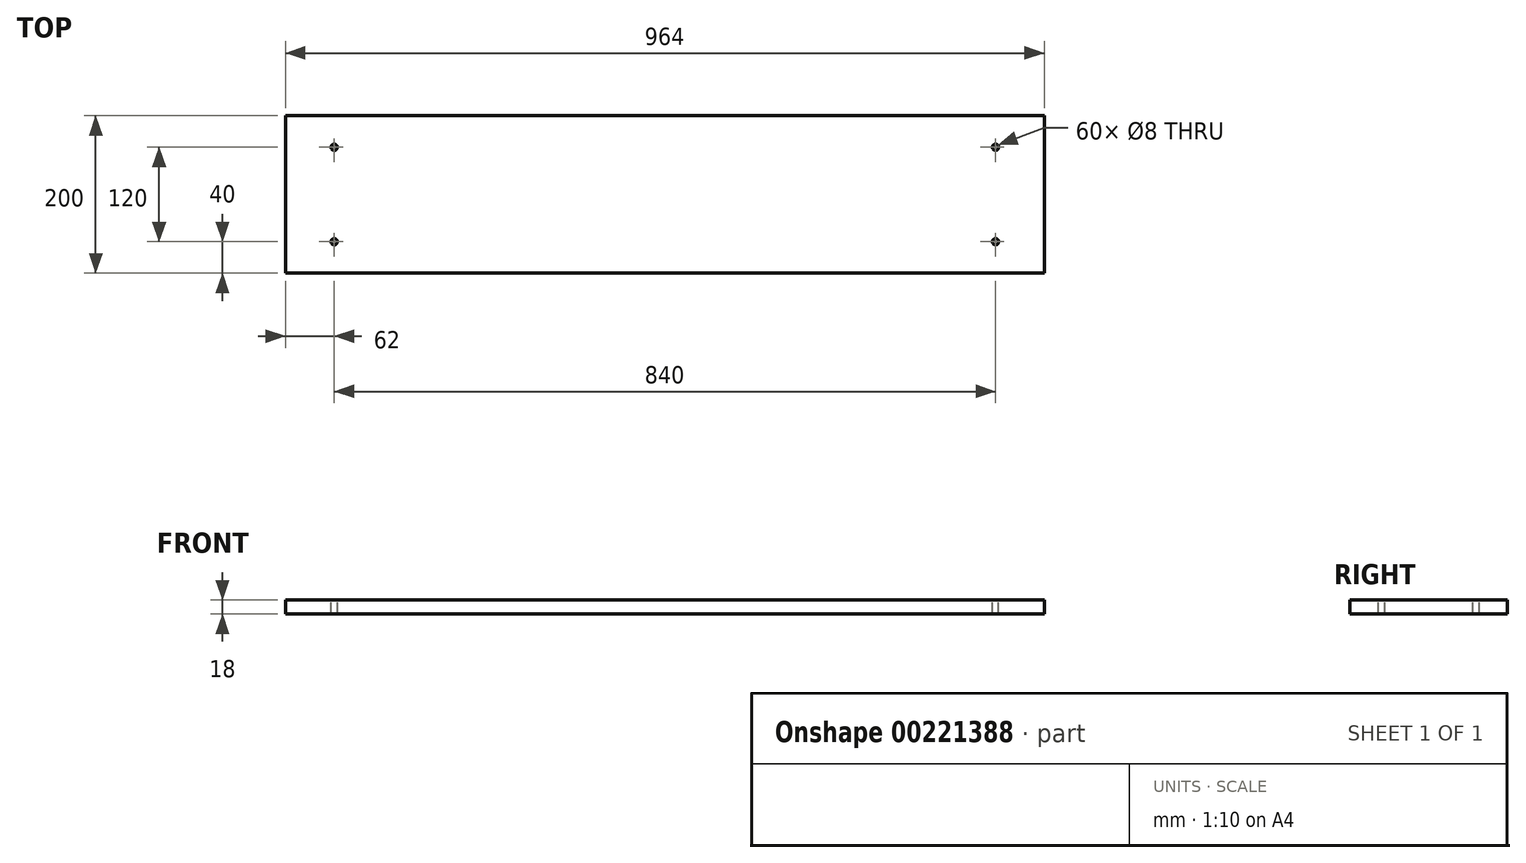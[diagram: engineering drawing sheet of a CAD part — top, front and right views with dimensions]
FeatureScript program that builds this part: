
annotation { "Feature Type Name" : "Feature", "Feature Type Description" : "" }
export const myFeature = defineFeature(function(context is Context, id is Id, definition is map)
    precondition{}
    {
        {
            var Q0;
            Q0=qCreatedBy(makeId("Top.planeOp"),FACE);
            var sketch = newSketch(context, id + "F0", { "sketchPlane" : qUnion([Q0])});
            skLineSegment(sketch, "E0.bottom", {"start": v(482, -100) * mm, "end": v(-482, -100) * mm});
            skLineSegment(sketch, "E0.top", {"start": v(482, 100) * mm, "end": v(-482, 100) * mm});
            skLineSegment(sketch, "E0.left", {"start": v(482, -100) * mm, "end": v(482, 100) * mm});
            skLineSegment(sketch, "E0.right", {"start": v(-482, -100) * mm, "end": v(-482, 100) * mm});
            skPoint(sketch, "E0.middle", {"position": v(0, 0) * mm});
            skSolve(sketch);
        }
        {
            var Q0;
            Q0=qSketchRegion(id+"F0",true);
            extrude(context, id + "F1", {"entities" : qUnion([Q0]), "depth" : 18 * mm});
        }
        {
            var Q0;
            Q0=makeQuery(id+"F1.opExtrude","CAP_FACE",FACE,{"disambiguationData":[OSD([sQuery(id+"F0.wireOp",EDGE,"E0.bottom"),sQuery(id+"F0.wireOp",EDGE,"E0.top"),sQuery(id+"F0.wireOp",EDGE,"E0.left"),sQuery(id+"F0.wireOp",EDGE,"E0.right")])],"isStart":false});
            var sketch = newSketch(context, id + "F2", { "sketchPlane" : qUnion([Q0])});
            skCircle(sketch, "E1", {"center": v(-420, 60) * mm, "radius": 4 * mm});
            skCircle(sketch, "E2", {"center": v(-420, -60) * mm, "radius": 4 * mm});
            skCircle(sketch, "E3", {"center": v(420, 60) * mm, "radius": 4 * mm});
            skCircle(sketch, "E4", {"center": v(420, -60) * mm, "radius": 4 * mm});
            skSolve(sketch);
        }
        {
            var Q0;
            Q0 = qSketchRegion(id + "F2", true);
            extrude(context, id + "F3", {"entities" : qUnion([Q0]), "operationType" : NewBodyOperationType.REMOVE, "oppositeDirection" : true, "depth" : 25 * mm});
        }
    });
